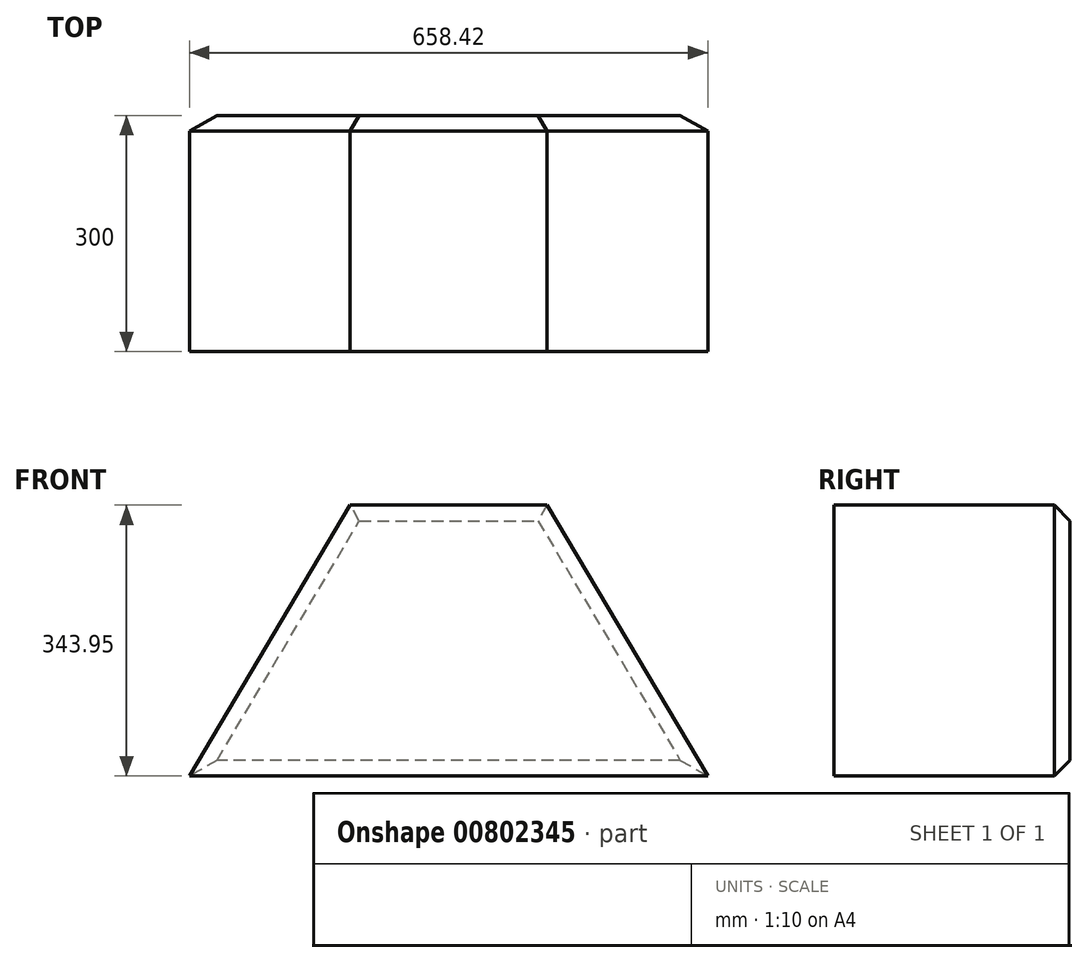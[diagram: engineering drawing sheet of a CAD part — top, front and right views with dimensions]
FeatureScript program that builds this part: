
annotation { "Feature Type Name" : "Feature", "Feature Type Description" : "" }
export const myFeature = defineFeature(function(context is Context, id is Id, definition is map)
    precondition{}
    {
        {
            var Q0;
            Q0=qCreatedBy(makeId("Front.planeOp"),FACE);
            var sketch = newSketch(context, id + "F0", { "sketchPlane" : qUnion([Q0])});
            skLineSegment(sketch, "E0", {"start": v(0, 0) * mm, "end": v(-125, 0) * mm});
            skLineSegment(sketch, "E1", {"start": v(-125, 0) * mm, "end": v(-329.2, -343.95) * mm});
            skLineSegment(sketch, "E2", {"start": v(-329.2, -343.95) * mm, "end": v(0, -343.95) * mm});
            skLineSegment(sketch, "E3", {"start": v(0, 0) * mm, "end": v(0, -343.95) * mm});
            skLineSegment(sketch, "E4.MirrorCS", {"start": v(125, 0) * mm, "end": v(329.2, -343.95) * mm});
            skLineSegment(sketch, "E5.MirrorCS", {"start": v(329.2, -343.95) * mm, "end": v(0, -343.95) * mm});
            skLineSegment(sketch, "E6.MirrorCS", {"start": v(0, 0) * mm, "end": v(125, 0) * mm});
            skSolve(sketch);
        }
        {
            var Q0;
            Q0 = qSketchRegion(id + "F0", true);
            extrude(context, id + "F1", {"entities" : qUnion([Q0]), "depth" : 300 * mm, "offsetDistance" : 25 * mm});
        }
        {
            var Q0;
            Q0=makeQuery(id+"F1.opExtrude","CAP_FACE",FACE,{"disambiguationData":[OSD([sQuery(id+"F0.wireOp",EDGE,"E0"),sQuery(id+"F0.wireOp",EDGE,"E1"),sQuery(id+"F0.wireOp",EDGE,"E2"),sQuery(id+"F0.wireOp",EDGE,"E4.MirrorCS"),sQuery(id+"F0.wireOp",EDGE,"E5.MirrorCS"),sQuery(id+"F0.wireOp",EDGE,"E6.MirrorCS")])],"isStart":true});
            chamfer(context, id + "F2", {"entities" : qUnion([Q0]), "width" : 20 * mm, "tangentPropagation" : true});
        }
    });
